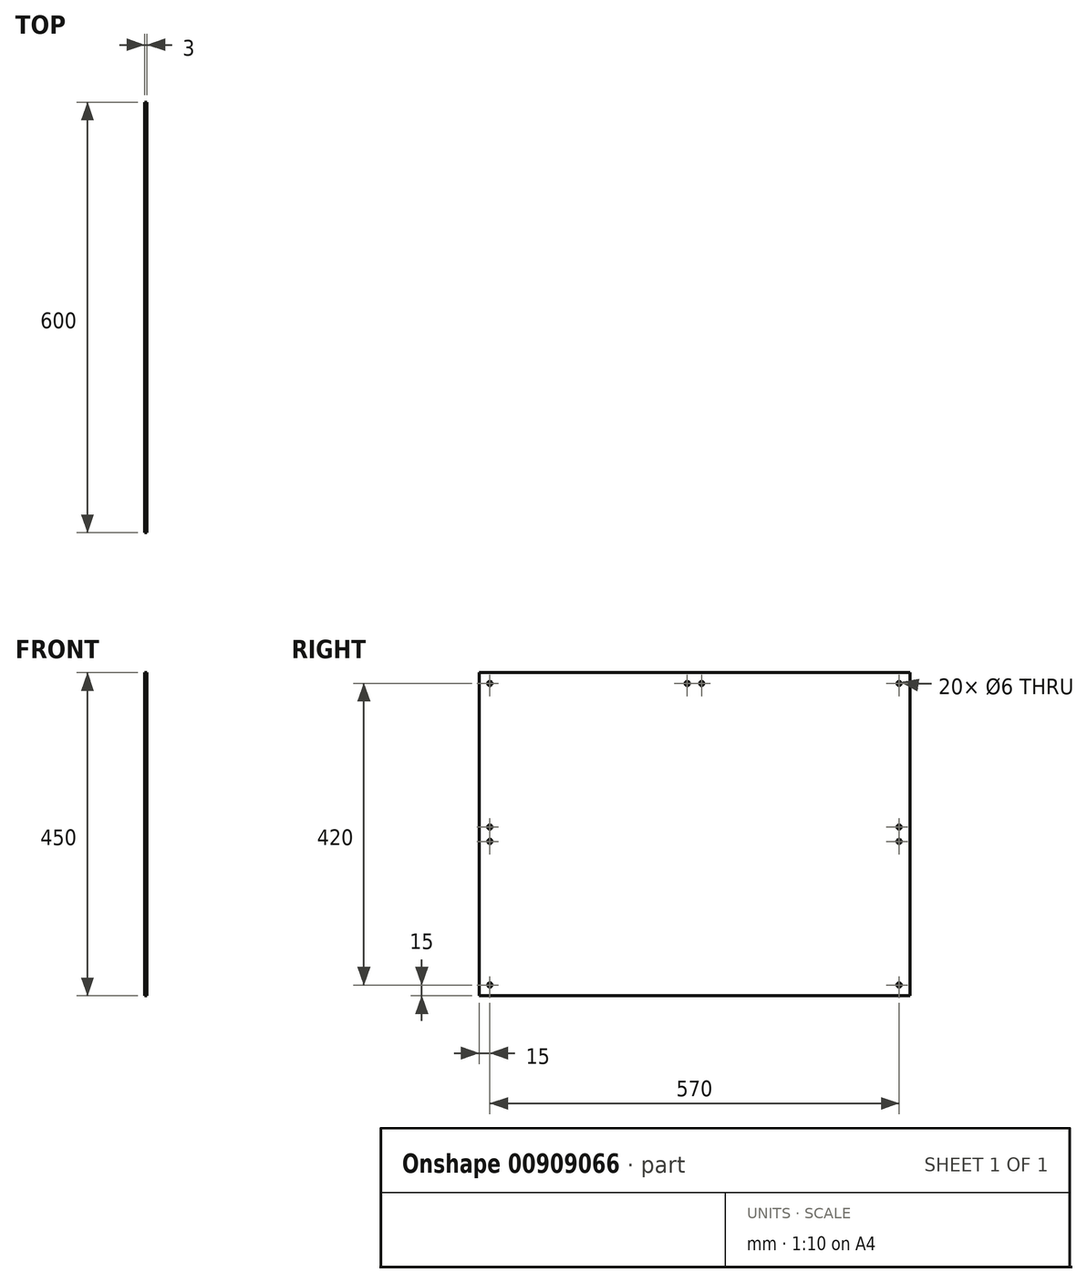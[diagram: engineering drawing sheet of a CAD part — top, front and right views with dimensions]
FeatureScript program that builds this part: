
annotation { "Feature Type Name" : "Feature", "Feature Type Description" : "" }
export const myFeature = defineFeature(function(context is Context, id is Id, definition is map)
    precondition{}
    {
        {
            var Q0;
            Q0=qCreatedBy(makeId("Right.planeOp"),FACE);
            var sketch = newSketch(context, id + "F0", { "sketchPlane" : qUnion([Q0])});
            skLineSegment(sketch, "E0.bottom", {"start": v(0, 0) * mm, "end": v(600, 0) * mm});
            skLineSegment(sketch, "E0.top", {"start": v(0, 450) * mm, "end": v(600, 450) * mm});
            skLineSegment(sketch, "E0.left", {"start": v(0, 0) * mm, "end": v(0, 450) * mm});
            skLineSegment(sketch, "E0.right", {"start": v(600, 0) * mm, "end": v(600, 450) * mm});
            skCircle(sketch, "E1", {"center": v(15, 15) * mm, "radius": 3 * mm});
            skCircle(sketch, "E2", {"center": v(585, 15) * mm, "radius": 3 * mm});
            skCircle(sketch, "E3", {"center": v(15, 435) * mm, "radius": 3 * mm});
            skCircle(sketch, "E4", {"center": v(585, 435) * mm, "radius": 3 * mm});
            skCircle(sketch, "E5", {"center": v(290, 435) * mm, "radius": 3 * mm});
            skCircle(sketch, "E6", {"center": v(310, 435) * mm, "radius": 3 * mm});
            skCircle(sketch, "E7", {"center": v(15, 235) * mm, "radius": 3 * mm});
            skCircle(sketch, "E8", {"center": v(15, 215) * mm, "radius": 3 * mm});
            skCircle(sketch, "E9", {"center": v(585, 235) * mm, "radius": 3 * mm});
            skCircle(sketch, "E10", {"center": v(585, 215) * mm, "radius": 3 * mm});
            skSolve(sketch);
        }
        {
            var Q0;
            Q0=makeQuery(id+"F0.imprint","IMPRINT",FACE,{"disambiguationData":[TD([[makeQuery(id+"F0.imprint","IMPRINT",EDGE,{"derivedFrom":sQuery(id+"F0.wireOp",EDGE,"E0.bottom")}),1.0]])]});
            extrude(context, id + "F1", {"entities" : qUnion([Q0]), "depth" : 3 * mm, "offsetDistance" : 25 * mm});
        }
    });
